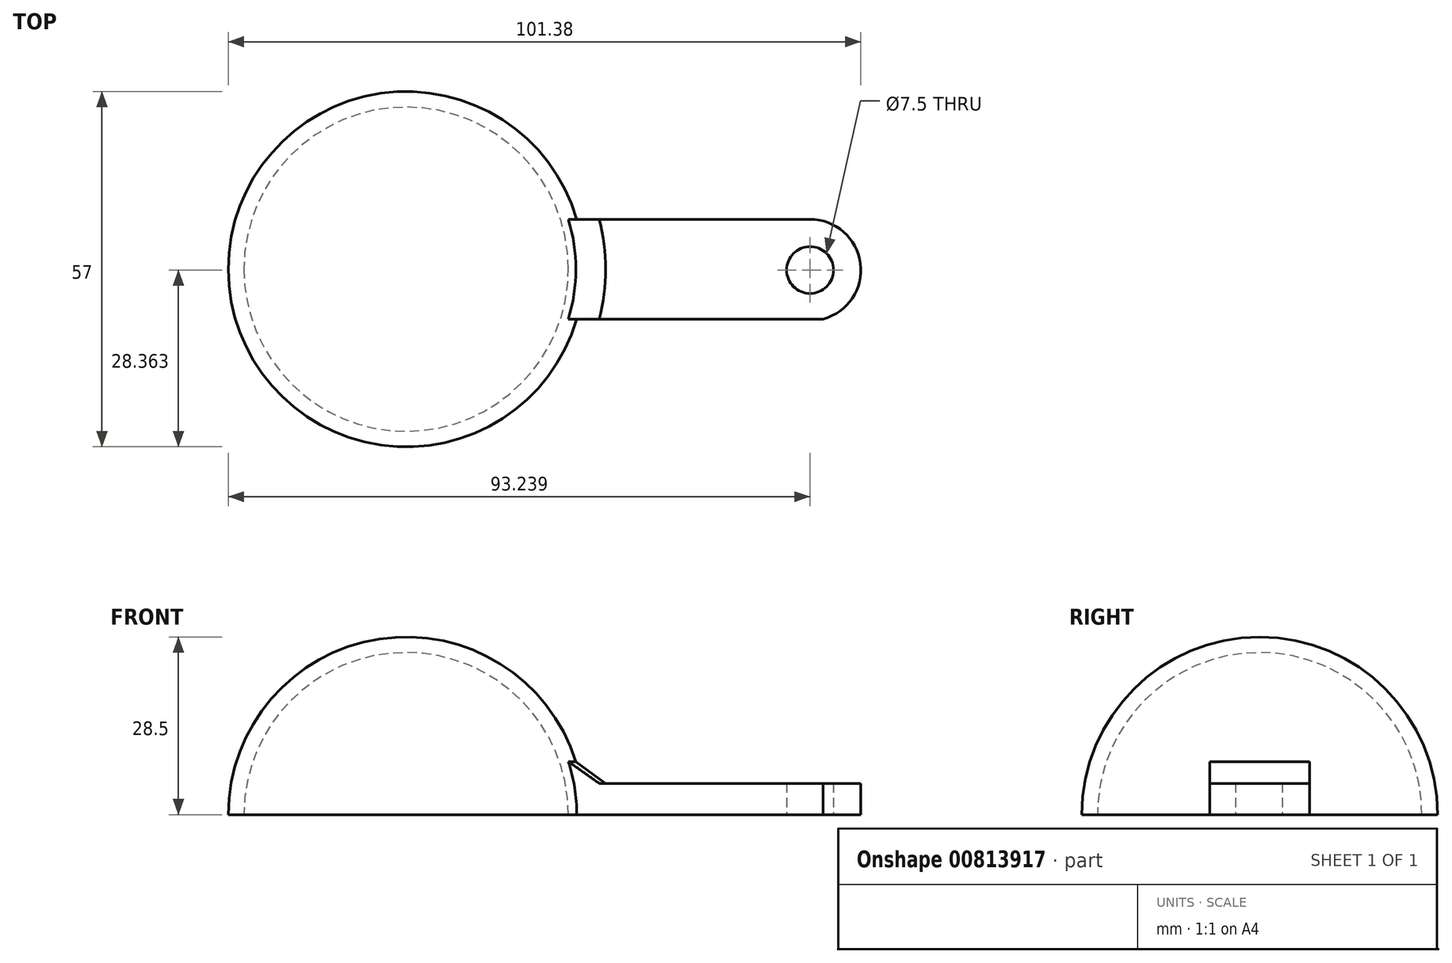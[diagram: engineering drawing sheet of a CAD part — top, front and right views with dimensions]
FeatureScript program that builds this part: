
annotation { "Feature Type Name" : "Feature", "Feature Type Description" : "" }
export const myFeature = defineFeature(function(context is Context, id is Id, definition is map)
    precondition{}
    {
        {
            var Q0;
            Q0=qCreatedBy(makeId("Top.planeOp"),FACE);
            var sketch = newSketch(context, id + "F0", { "sketchPlane" : qUnion([Q0])});
            skCircle(sketch, "E0", {"center": v(0, 0) * mm, "radius": 26 * mm});
            skLineSegment(sketch, "E1", {"start": v(-26, 0) * mm, "end": v(26, 0) * mm});
            skCircle(sketch, "E2.0", {"center": v(0, 0) * mm, "radius": 28.5 * mm});
            skLineSegment(sketch, "E3", {"start": v(-26, 0) * mm, "end": v(-28.5, 0) * mm});
            skLineSegment(sketch, "E4", {"start": v(26, 0) * mm, "end": v(28.5, 0) * mm});
            skSolve(sketch);
        }
        {
            var Q0;
            {var subQ0=sQuery(id+"F0.wireOp",EDGE,"E3");Q0=makeQuery(id+"F0.imprint","IMPRINT",FACE,{"disambiguationData":[TD([[makeQuery(id+"F0.imprint","IMPRINT",EDGE,{"derivedFrom":subQ0}),-1.0]])]});}
            var Q1;
            Q1=sQuery(id+"F0.wireOp",EDGE,"E1");
            revolve(context, id + "F1", {"surfaceOperationType" : NewSurfaceOperationType.NEW, "entities" : qUnion([Q0]), "axis" : qUnion([Q1]), "revolveType" : RevolveType.ONE_DIRECTION, "angle" : 180 * degree});
        }
        {
            var Q0;
            Q0=qCreatedBy(makeId("Top.planeOp"),FACE);
            var sketch = newSketch(context, id + "F2", { "sketchPlane" : qUnion([Q0])});
            skLineSegment(sketch, "E5", {"start": v(24.74, 8) * mm, "end": v(64.74, 8) * mm});
            skLineSegment(sketch, "E6", {"start": v(66.83, -8) * mm, "end": v(24.74, -8) * mm});
            skArc(sketch, "E7", {"start": v(66.83, -8) * mm, "mid": v(72.8, 0.92) * mm, "end": v(64.74, 8) * mm});
            skCircle(sketch, "E8", {"center": v(0, 0) * mm, "radius": 26 * mm});
            skCircle(sketch, "E9", {"center": v(64.74, -0.14) * mm, "radius": 3.75 * mm});
            skSolve(sketch);
        }
        {
            var Q0;
            {var subQ0=sQuery(id+"F2.wireOp",EDGE,"E5");Q0=makeQuery(id+"F2.imprint","IMPRINT",FACE,{"disambiguationData":[TD([[makeQuery(id+"F2.imprint","IMPRINT",EDGE,{"derivedFrom":subQ0}),-1.0]])]});}
            var Q1;
            {var subQ0=sQuery(id+"F2.wireOp",EDGE,"YslB7Wh7-oUDE-qH7j-q6ka-ur2prJoxq0ld");Q1=makeQuery(id+"F2.imprint","IMPRINT",FACE,{"disambiguationData":[TD([[makeQuery(id+"F2.imprint","IMPRINT",EDGE,{"derivedFrom":subQ0}),-1.0]])]});}
            var Q2;
            {var subQ0=sQuery(id+"F2.wireOp",EDGE,"YslB7Wh7-oUDE-qH7j-q6ka-ur2prJoxq0ld");Q2=makeQuery(id+"F2.imprint","IMPRINT",FACE,{"disambiguationData":[TD([[makeQuery(id+"F2.imprint","IMPRINT",EDGE,{"derivedFrom":subQ0}),1.0]])]});}
            extrude(context, id + "F3", {"entities" : qUnion([Q0, Q1, Q2]), "operationType" : NewBodyOperationType.ADD, "depth" : 5 * mm, "offsetDistance" : 25 * mm});
        }
        {
            var Q0;
            Q0=makeQuery(id+"F3.boolean.opBoolean","INTERSECT",EDGE,{"derivedFrom":[makeQuery(id+"F1.opRevolve","SWEPT_FACE",FACE,{"disambiguationData":[OSD([sQuery(id+"F0.wireOp",EDGE,"E2.0")])]}),makeQuery(id+"F3.opExtrude","CAP_FACE",FACE,{"disambiguationData":[OSD([sQuery(id+"F2.wireOp",EDGE,"E5"),sQuery(id+"F2.wireOp",EDGE,"E6"),sQuery(id+"F2.wireOp",EDGE,"E7"),sQuery(id+"F2.wireOp",EDGE,"E8")])],"isStart":false})]});
            chamfer(context, id + "F4", {"entities" : qUnion([Q0]), "width" : 5 * mm, "tangentPropagation" : true});
        }
    });
